# Revit family: ToothbrushHolder-Vitra-BaseSeries-A44145
name_source: partatom
category: Plumbing Fixtures
revit_build: Autodesk Revit 2017 (Build: 20160225_1515(x64)
units: mm (PartAtom-declared; Revit-internal decimal feet)

## family parameters
Cut with Voids When Loaded = No
Host = Face
OmniClass Number = 23.45.00.00
OmniClass Title = Sanitary, Laundry, and Cleaning Equipment
Part Type = Normal
Room Calculation Point = No
Round Connector Dimension = Use Diameter
Shared = Yes

## types (1)
- ToothbrushHolder-Vitra-BaseSeries-A44145
    Article No. (default) = A44145
    BIMobject category = Sanitary - Accessories
    Brand = VitrA
    CW Connection = No
    Coating Material = Glass
    Color = Chrome
    Default Elevation = 1200 mm
    Description = Base Toothbrush Holder
    Design country = Turkey
    HW Connection = No
    IFC Classification = Sanitary Terminal
    Main Material = Glass
    Manufacturer = Vitra
    Manufacturer name = Vitra
    Masterformat 2014 Code = 10 28 16
    Masterformat 2014 Description = Bath Accessories
    Model = A44145
    Mounting type = Wall Mounted
    NBS Referans Code = 35-75-89
    NBS Referans Description = Toothbrush Holders
    Nominal Depth (mm) = 70 mm  [stored 0.229659 ft]
    Nominal Height (mm) = 115 mm  [stored 0.377297 ft]
    Nominal Width (mm) = 70 mm  [stored 0.229659 ft]
    OmniClass Code = 23-31 25 00
    OmniClass Description = Toilet and Bath Specialties
    Primary Material = Chrome
    Product SKU = A44145
    Product Type = Built-in Toothbrush Holder
    Product certification = https://www.vitraglobal.com
    Product family = BaseSeries
    Product group = Toothbrush Holder
    Product url = https://vitraglobal.com
    Technical description = https://vitraglobal.com
    UNSPSC Description = Furniture and Furnishings
    URL = https://vitraglobal.com
    Uniclass 1.4 Code = L824
    Uniclass 1.4 Description = Bathroom, toilet furniture and fittings
    Uniclass 2.0 Code = PR-35-75-89
    Uniclass 2.0 Description = Toothbrush Holders
    Uniclass 2015 Code = Pr_40_20_76_89
    Uniclass 2015 Name = Toothbrush holders
    Uniformat II Code = E20
    Uniformat II Description = FURNISHINGS
    Vent Connection = No
    Warranty Period (Year) = 5 Years
    Waste Connection = No
    Weight Net (kg) = 1
    Youtube = https://www.youtube.com

note: [stored X ft] marks values corroborated as IEEE doubles in the binary element streams (Revit-internal decimal feet)

## geometry (parser evidence)
native form markers: Sweep x3
no freeform markers — native parametric forms only
